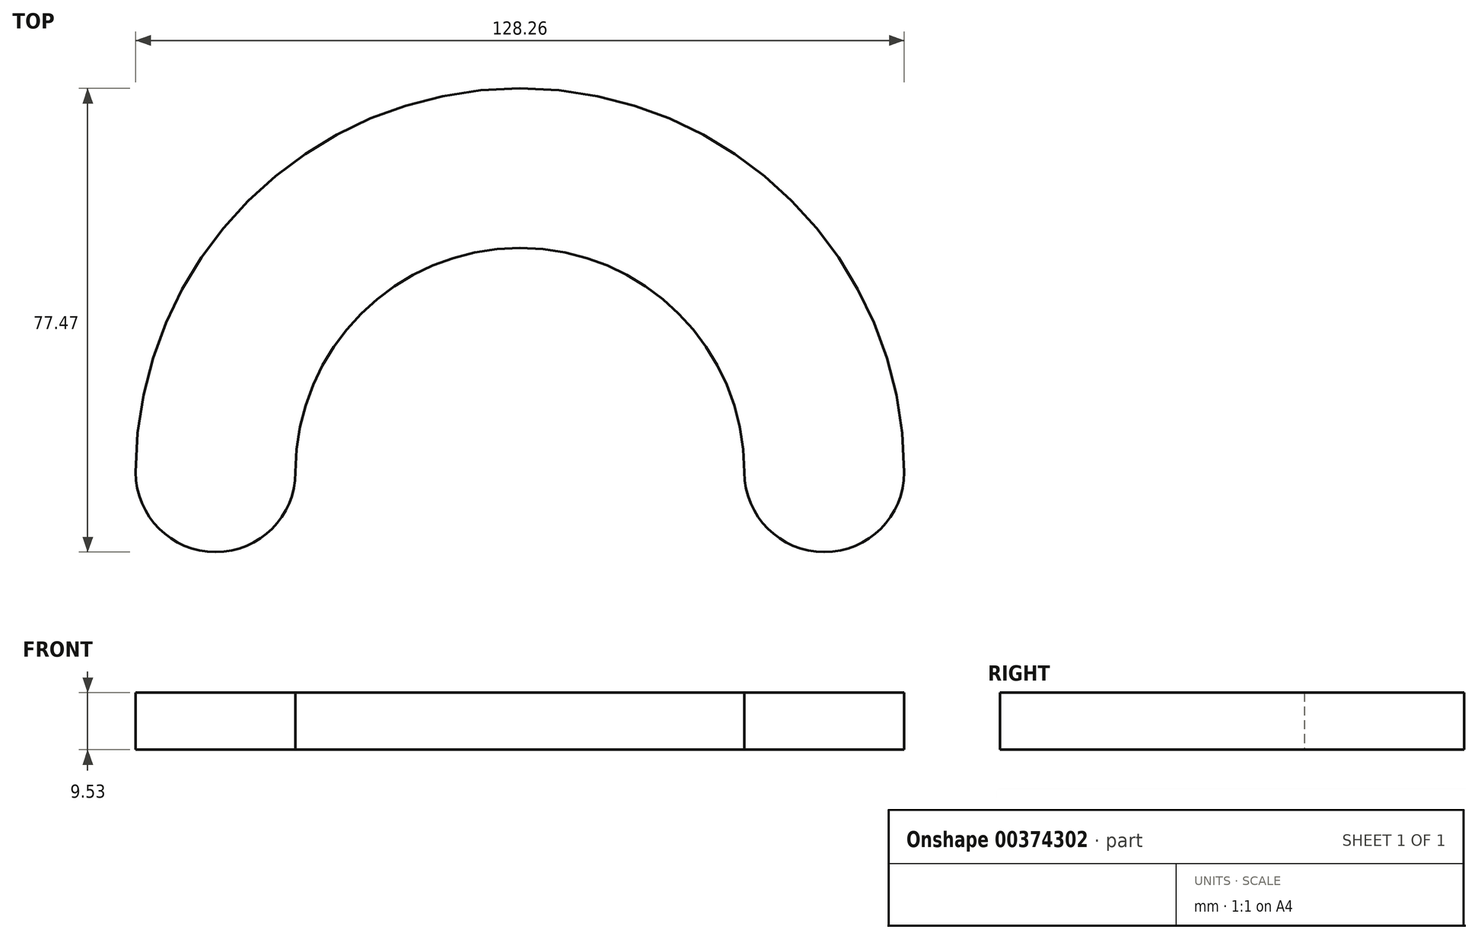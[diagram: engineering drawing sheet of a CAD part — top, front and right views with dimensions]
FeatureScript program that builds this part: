
annotation { "Feature Type Name" : "Feature", "Feature Type Description" : "" }
export const myFeature = defineFeature(function(context is Context, id is Id, definition is map)
    precondition{}
    {
        {
            var Q0;
            Q0=qCreatedBy(makeId("Top.planeOp"),FACE);
            var sketch = newSketch(context, id + "F0", { "sketchPlane" : qUnion([Q0])});
            skArc(sketch, "E0", {"start": v(-64.14, 0) * mm, "mid": v(-50.8, -13.34) * mm, "end": v(-37.47, 0) * mm});
            skArc(sketch, "E1", {"start": v(37.47, 0) * mm, "mid": v(50.8, -13.34) * mm, "end": v(64.14, 0) * mm});
            skArc(sketch, "E2", {"start": v(37.46, 0) * mm, "mid": v(0, 37.46) * mm, "end": v(-37.46, 0) * mm});
            skArc(sketch, "E3", {"start": v(64.13, 0) * mm, "mid": v(0, 64.13) * mm, "end": v(-64.13, 0) * mm});
            skSolve(sketch);
        }
        {
            var Q0;
            Q0=makeQuery(id+"F0.imprint","IMPRINT",FACE,{"disambiguationData":[TD([[makeQuery(id+"F0.imprint","IMPRINT",EDGE,{"derivedFrom":sQuery(id+"F0.wireOp",EDGE,"E0")}),1.0]])]});
            extrude(context, id + "F1", {"entities" : qUnion([Q0]), "depth" : 9.52 * mm, "offsetDistance" : 25.4 * mm});
        }
    });
